# Revit family: ГРЕЕРС ЗВ - 200 В
name_source: partatom
category: Wyposażenie mechaniczne
revit_build: Autodesk Revit 2016 (Build: 20150220_1215(x64)
units: mm (PartAtom-declared; Revit-internal decimal feet)

## family parameters
Obiekt nadrzędny = Powierzchnia
Punkt obliczania pomieszczeń = Nie
Tnij formami wycięć po wczytaniu = Nie
Typ części = Normalny
Współdzielony = Nie
Wymiar okrągłego złącza = Użyj średnicy

## types (60) — shared parameters
Bec аппарата, наполненного водой = 38.50 kg
Domyślna rzędna = 2200 mm
IP = 21
Model = ГРЕЕРС ЗВ - 200 В
Opis = Воздушная завеса
Producent = ГРЕЕРС
Автор = www.archispace.com
Вентилятор = Однофазный двигатель с поперечным ротором
Вес аппарата = 35.10 kg
Данные продукта = https://greers.ru
Длина = 2000 mm  [stored 6.56168 ft]
Классификация нагрузки = ДВИГАТЕЛЬ
Коэффициент мощности = 0.94
Макс. потребление тока = 1 A
Материал = ГРЕЕРС-сталь-белый
Материал 2 = ГРЕЕРС-сталь,перфорация-белый
Напряжение питания = 230 V
Патрубки = 3/4"
Полная мощность = 276 VA

## per-type parameters (varying)
| type | Tемпература воды на выходе из теплообменника (Tw2) | Количество воды проходящей через теплообменник | Падение давления воды в теплообменнике | Производительность | Температура воды на входе в теплообменник (Tw1) | Температура воздуха на входе в аппарат (Тр1) | Температура воздуха на выходе из аппарата (Тр2) | Тепловая мощность |
| ГРЕЕРС ЗВ - 200 В, 1 скорость, Tw1/Tw2 = 90/70°C, Tp1 = 0 | 70 °C | 0.385 L/s | 39.4 kPa | 2300 m³/h | 90 °C | 0 °C | 40.5 °C | 31.4 kW |
| ГРЕЕРС ЗВ - 200 В, 1 скорость, Tw1/Tw2 = 90/70°C, Tp1 = 5 | 70 °C | 0.361 L/s | 35.1 kPa | 2300 m³/h | 90 °C | 5 °C | 43 °C | 29.5 kW |
| ГРЕЕРС ЗВ - 200 В, 1 скорость, Tw1/Tw2 = 90/70°C, Tp1 = 10 | 70 °C | 0.337 L/s | 31 kPa | 2300 m³/h | 90 °C | 10 °C | 45 °C | 27.5 kW |
| ГРЕЕРС ЗВ - 200 В, 1 скорость, Tw1/Tw2 = 90/70°C, Tp1 = 15 | 70 °C | 0.313 L/s | 27.1 kPa | 2300 m³/h | 90 °C | 15 °C | 47.5 °C | 25.6 kW |
| ГРЕЕРС ЗВ - 200 В, 1 скорость, Tw1/Tw2 = 90/70°C, Tp1 = 20 | 70 °C | 0.289 L/s | 23.4 kPa | 2300 m³/h | 90 °C | 20 °C | 50 °C | 23.6 kW |
| ГРЕЕРС ЗВ - 200 В, 1 скорость, Tw1/Tw2 = 80/60°C, Tp1 = 0 | 60 °C | 0.332 L/s | 30.9 kPa | 2300 m³/h | 80 °C | 0 °C | 35 °C | 27.2 kW |
| ГРЕЕРС ЗВ - 200 В, 1 скорость, Tw1/Tw2 = 80/60°C, Tp1 = 5 | 60 °C | 0.308 L/s | 27 kPa | 2300 m³/h | 80 °C | 5 °C | 37.5 °C | 25.2 kW |
| ГРЕЕРС ЗВ - 200 В, 1 скорость, Tw1/Tw2 = 80/60°C, Tp1 = 10 | 60 °C | 0.284 L/s | 23.3 kPa | 2300 m³/h | 80 °C | 10 °C | 40 °C | 23.3 kW |
| ГРЕЕРС ЗВ - 200 В, 1 скорость, Tw1/Tw2 = 80/60°C, Tp1 = 15 | 60 °C | 0.26 L/s | 19.9 kPa | 2300 m³/h | 80 °C | 15 °C | 42 °C | 21.3 kW |
| ГРЕЕРС ЗВ - 200 В, 1 скорость, Tw1/Tw2 = 80/60°C, Tp1 = 20 | 60 °C | 0.235 L/s | 16.6 kPa | 2300 m³/h | 80 °C | 20 °C | 44.5 °C | 19.3 kW |
| ГРЕЕРС ЗВ - 200 В, 1 скорость, Tw1/Tw2 = 70/50°C, Tp1 = 0 | 50 °C | 0.279 L/s | 23.3 kPa | 2300 m³/h | 70 °C | 0 °C | 29.5 °C | 22.9 kW |
| ГРЕЕРС ЗВ - 200 В, 1 скорость, Tw1/Tw2 = 70/50°C, Tp1 = 5 | 50 °C | 0.255 L/s | 19.8 kPa | 2300 m³/h | 70 °C | 5 °C | 32 °C | 21 kW |
| ГРЕЕРС ЗВ - 200 В, 1 скорость, Tw1/Tw2 = 70/50°C, Tp1 = 10 | 50 °C | 0.23 L/s | 16.6 kPa | 2300 m³/h | 70 °C | 10 °C | 34.5 °C | 19 kW |
| ГРЕЕРС ЗВ - 200 В, 1 скорость, Tw1/Tw2 = 70/50°C, Tp1 = 15 | 50 °C | 0.206 L/s | 13.6 kPa | 2300 m³/h | 70 °C | 15 °C | 36.5 °C | 17 kW |
| ГРЕЕРС ЗВ - 200 В, 1 скорость, Tw1/Tw2 = 70/50°C, Tp1 = 20 | 50 °C | 0.182 L/s | 10.8 kPa | 2300 m³/h | 70 °C | 20 °C | 39 °C | 14.9 kW |
| ГРЕЕРС ЗВ - 200 В, 1 скорость, Tw1/Tw2 = 60/40°C, Tp1 = 0 | 40 °C | 0.226 L/s | 16.6 kPa | 2300 m³/h | 60 °C | 0 °C | 24 °C | 18.7 kW |
| ГРЕЕРС ЗВ - 200 В, 1 скорость, Tw1/Tw2 = 60/40°C, Tp1 = 5 | 40 °C | 0.202 L/s | 13.6 kPa | 2300 m³/h | 60 °C | 5 °C | 26.5 °C | 16.7 kW |
| ГРЕЕРС ЗВ - 200 В, 1 скорость, Tw1/Tw2 = 60/40°C, Tp1 = 10 | 40 °C | 0.177 L/s | 10.8 kPa | 2300 m³/h | 60 °C | 10 °C | 29 °C | 14.7 kW |
| ГРЕЕРС ЗВ - 200 В, 1 скорость, Tw1/Tw2 = 60/40°C, Tp1 = 15 | 40 °C | 0.153 L/s | 8.3 kPa | 2300 m³/h | 60 °C | 15 °C | 31 °C | 12.6 kW |
| ГРЕЕРС ЗВ - 200 В, 1 скорость, Tw1/Tw2 = 60/40°C, Tp1 = 20 | 40 °C | 0.128 L/s | 6 kPa | 2300 m³/h | 60 °C | 20 °C | 33.5 °C | 10.6 kW |
| ГРЕЕРС ЗВ - 200 В, 2 скорость, Tw1/Tw2 = 90/70°C, Tp1 = 0 | 70 °C | 0.416 L/s | 45.4 kPa | 2600 m³/h | 90 °C | 0 °C | 38.5 °C | 34 kW |
| ГРЕЕРС ЗВ - 200 В, 2 скорость, Tw1/Tw2 = 90/70°C, Tp1 = 5 | 70 °C | 0.39 L/s | 40.5 kPa | 2600 m³/h | 90 °C | 5 °C | 41 °C | 31.9 kW |
| ГРЕЕРС ЗВ - 200 В, 2 скорость, Tw1/Tw2 = 90/70°C, Tp1 = 10 | 70 °C | 0.365 L/s | 35.7 kPa | 2600 m³/h | 90 °C | 10 °C | 43.5 °C | 29.8 kW |
| ГРЕЕРС ЗВ - 200 В, 2 скорость, Tw1/Tw2 = 90/70°C, Tp1 = 15 | 70 °C | 0.339 L/s | 31.2 kPa | 2600 m³/h | 90 °C | 15 °C | 46 °C | 27.6 kW |
| ГРЕЕРС ЗВ - 200 В, 2 скорость, Tw1/Tw2 = 90/70°C, Tp1 = 20 | 70 °C | 0.312 L/s | 26.9 kPa | 2600 m³/h | 90 °C | 20 °C | 48.5 °C | 25.5 kW |
| ГРЕЕРС ЗВ - 200 В, 2 скорость, Tw1/Tw2 = 80/60°C, Tp1 = 0 | 60 °C | 0.358 L/s | 35.6 kPa | 2600 m³/h | 80 °C | 0 °C | 33.5 °C | 29.4 kW |
| ГРЕЕРС ЗВ - 200 В, 2 скорость, Tw1/Tw2 = 80/60°C, Tp1 = 5 | 60 °C | 0.333 L/s | 31.1 kPa | 2600 m³/h | 80 °C | 5 °C | 36 °C | 27.3 kW |
| ГРЕЕРС ЗВ - 200 В, 2 скорость, Tw1/Tw2 = 80/60°C, Tp1 = 10 | 60 °C | 0.307 L/s | 26.9 kPa | 2600 m³/h | 80 °C | 10 °C | 38.5 °C | 25.1 kW |
| ГРЕЕРС ЗВ - 200 В, 2 скорость, Tw1/Tw2 = 80/60°C, Tp1 = 15 | 60 °C | 0.28 L/s | 22.9 kPa | 2600 m³/h | 80 °C | 15 °C | 41 °C | 23 kW |
| ГРЕЕРС ЗВ - 200 В, 2 скорость, Tw1/Tw2 = 80/60°C, Tp1 = 20 | 60 °C | 0.254 L/s | 19.1 kPa | 2600 m³/h | 80 °C | 20 °C | 43.5 °C | 20.8 kW |
| ГРЕЕРС ЗВ - 200 В, 2 скорость, Tw1/Tw2 = 70/50°C, Tp1 = 0 | 50 °C | 0.301 L/s | 26.8 kPa | 2600 m³/h | 70 °C | 0 °C | 28 °C | 24.8 kW |
| ГРЕЕРС ЗВ - 200 В, 2 скорость, Tw1/Tw2 = 70/50°C, Tp1 = 5 | 50 °C | 0.275 L/s | 22.8 kPa | 2600 m³/h | 70 °C | 5 °C | 30.5 °C | 22.7 kW |
| ГРЕЕРС ЗВ - 200 В, 2 скорость, Tw1/Tw2 = 70/50°C, Tp1 = 10 | 50 °C | 0.249 L/s | 19.1 kPa | 2600 m³/h | 70 °C | 10 °C | 33 °C | 20.5 kW |
| ГРЕЕРС ЗВ - 200 В, 2 скорость, Tw1/Tw2 = 70/50°C, Tp1 = 15 | 50 °C | 0.223 L/s | 15.6 kPa | 2600 m³/h | 70 °C | 15 °C | 35.5 °C | 18.3 kW |
| ГРЕЕРС ЗВ - 200 В, 2 скорость, Tw1/Tw2 = 70/50°C, Tp1 = 20 | 50 °C | 0.196 L/s | 12.4 kPa | 2600 m³/h | 70 °C | 20 °C | 38 °C | 16.1 kW |
| ГРЕЕРС ЗВ - 200 В, 2 скорость, Tw1/Tw2 = 60/40°C, Tp1 = 0 | 40 °C | 0.244 L/s | 19.1 kPa | 2600 m³/h | 60 °C | 0 °C | 23 °C | 20.2 kW |
| ГРЕЕРС ЗВ - 200 В, 2 скорость, Tw1/Tw2 = 60/40°C, Tp1 = 5 | 40 °C | 0.218 L/s | 15.6 kPa | 2600 m³/h | 60 °C | 5 °C | 25.5 °C | 18 kW |
| ГРЕЕРС ЗВ - 200 В, 2 скорость, Tw1/Tw2 = 60/40°C, Tp1 = 10 | 40 °C | 0.192 L/s | 12.4 kPa | 2600 m³/h | 60 °C | 10 °C | 28 °C | 15.9 kW |
| ГРЕЕРС ЗВ - 200 В, 2 скорость, Tw1/Tw2 = 60/40°C, Tp1 = 15 | 40 °C | 0.165 L/s | 9.5 kPa | 2600 m³/h | 60 °C | 15 °C | 30.5 °C | 13.6 kW |
| ГРЕЕРС ЗВ - 200 В, 2 скорость, Tw1/Tw2 = 60/40°C, Tp1 = 20 | 40 °C | 0.138 L/s | 6.9 kPa | 2600 m³/h | 60 °C | 20 °C | 33 °C | 11.4 kW |
| ГРЕЕРС ЗВ - 200 В, 3 скорость, Tw1/Tw2 = 90/70°C, Tp1 = 0 | 70 °C | 0.455 L/s | 53.5 kPa | 3000 m³/h | 90 °C | 0 °C | 36.5 °C | 37.1 kW |
| ГРЕЕРС ЗВ - 200 В, 3 скорость, Tw1/Tw2 = 90/70°C, Tp1 = 5 | 70 °C | 0.427 L/s | 47.6 kPa | 3000 m³/h | 90 °C | 5 °C | 39.5 °C | 34.8 kW |
| ГРЕЕРС ЗВ - 200 В, 3 скорость, Tw1/Tw2 = 90/70°C, Tp1 = 10 | 70 °C | 0.399 L/s | 42 kPa | 3000 m³/h | 90 °C | 10 °C | 42 °C | 32.5 kW |
| ГРЕЕРС ЗВ - 200 В, 3 скорость, Tw1/Tw2 = 90/70°C, Tp1 = 15 | 70 °C | 0.37 L/s | 36.7 kPa | 3000 m³/h | 90 °C | 15 °C | 44.5 °C | 30.2 kW |
| ГРЕЕРС ЗВ - 200 В, 3 скорость, Tw1/Tw2 = 90/70°C, Tp1 = 20 | 70 °C | 0.341 L/s | 31.7 kPa | 3000 m³/h | 90 °C | 20 °C | 47 °C | 27.9 kW |
| ГРЕЕРС ЗВ - 200 В, 3 скорость, Tw1/Tw2 = 80/60°C, Tp1 = 0 | 60 °C | 0.392 L/s | 41.9 kPa | 3000 m³/h | 80 °C | 0 °C | 31.5 °C | 32.1 kW |
| ГРЕЕРС ЗВ - 200 В, 3 скорость, Tw1/Tw2 = 80/60°C, Tp1 = 5 | 60 °C | 0.364 L/s | 36.6 kPa | 3000 m³/h | 80 °C | 5 °C | 34.5 °C | 29.8 kW |
| ГРЕЕРС ЗВ - 200 В, 3 скорость, Tw1/Tw2 = 80/60°C, Tp1 = 10 | 60 °C | 0.335 L/s | 31.6 kPa | 3000 m³/h | 80 °C | 10 °C | 37 °C | 27.5 kW |
| ГРЕЕРС ЗВ - 200 В, 3 скорость, Tw1/Tw2 = 80/60°C, Tp1 = 15 | 60 °C | 0.307 L/s | 26.8 kPa | 3000 m³/h | 80 °C | 15 °C | 39.5 °C | 25.1 kW |
| ГРЕЕРС ЗВ - 200 В, 3 скорость, Tw1/Tw2 = 80/60°C, Tp1 = 20 | 60 °C | 0.278 L/s | 22.4 kPa | 3000 m³/h | 80 °C | 20 °C | 42 °C | 22.8 kW |
| ГРЕЕРС ЗВ - 200 В, 3 скорость, Tw1/Tw2 = 70/50°C, Tp1 = 0 | 50 °C | 0.329 L/s | 31.5 kPa | 3000 m³/h | 70 °C | 0 °C | 26.5 °C | 27.1 kW |
| ГРЕЕРС ЗВ - 200 В, 3 скорость, Tw1/Tw2 = 70/50°C, Tp1 = 5 | 50 °C | 0.301 L/s | 26.8 kPa | 3000 m³/h | 70 °C | 5 °C | 29.5 °C | 24.8 kW |
| ГРЕЕРС ЗВ - 200 В, 3 скорость, Tw1/Tw2 = 70/50°C, Tp1 = 10 | 50 °C | 0.272 L/s | 22.4 kPa | 3000 m³/h | 70 °C | 10 °C | 32 °C | 22.4 kW |
| ГРЕЕРС ЗВ - 200 В, 3 скорость, Tw1/Tw2 = 70/50°C, Tp1 = 15 | 50 °C | 0.244 L/s | 18.2 kPa | 3000 m³/h | 70 °C | 15 °C | 34.5 °C | 20 kW |
| ГРЕЕРС ЗВ - 200 В, 3 скорость, Tw1/Tw2 = 70/50°C, Tp1 = 20 | 50 °C | 0.214 L/s | 14.6 kPa | 3000 m³/h | 70 °C | 20 °C | 37 °C | 17.6 kW |
| ГРЕЕРС ЗВ - 200 В, 3 скорость, Tw1/Tw2 = 60/40°C, Tp1 = 0 | 40 °C | 0.267 L/s | 22.4 kPa | 3000 m³/h | 60 °C | 0 °C | 22 °C | 22 kW |
| ГРЕЕРС ЗВ - 200 В, 3 скорость, Tw1/Tw2 = 60/40°C, Tp1 = 5 | 40 °C | 0.239 L/s | 18.3 kPa | 3000 m³/h | 60 °C | 5 °C | 24.5 °C | 19.7 kW |
| ГРЕЕРС ЗВ - 200 В, 3 скорость, Tw1/Tw2 = 60/40°C, Tp1 = 10 | 40 °C | 0.21 L/s | 14.5 kPa | 3000 m³/h | 60 °C | 10 °C | 27 °C | 17.3 kW |
| ГРЕЕРС ЗВ - 200 В, 3 скорость, Tw1/Tw2 = 60/40°C, Tp1 = 15 | 40 °C | 0.181 L/s | 11.1 kPa | 3000 m³/h | 60 °C | 15 °C | 29.5 °C | 14.9 kW |
| ГРЕЕРС ЗВ - 200 В, 3 скорость, Tw1/Tw2 = 60/40°C, Tp1 = 20 | 40 °C | 0.151 L/s | 8.1 kPa | 3000 m³/h | 60 °C | 20 °C | 32 °C | 12.5 kW |

note: [stored X ft] marks values corroborated as IEEE doubles in the binary element streams (Revit-internal decimal feet)
